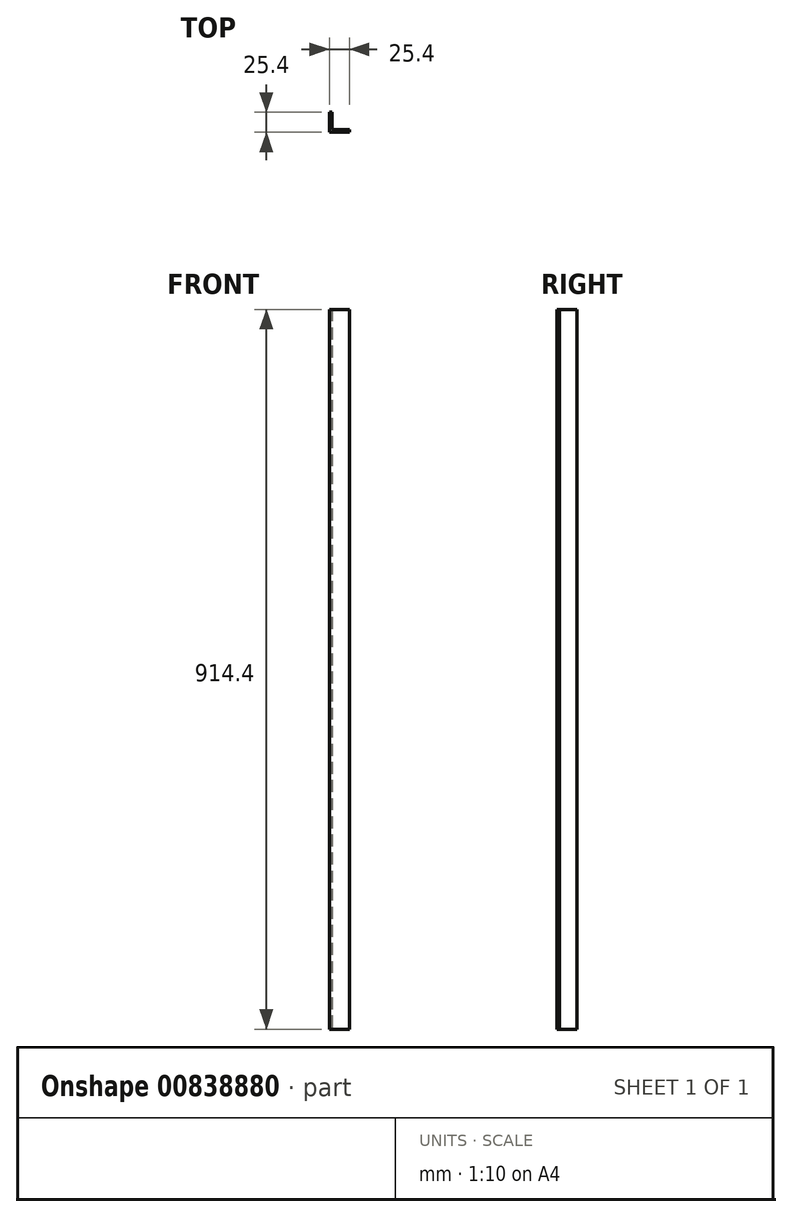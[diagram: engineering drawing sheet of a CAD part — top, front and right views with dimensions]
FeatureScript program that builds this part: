
annotation { "Feature Type Name" : "Feature", "Feature Type Description" : "" }
export const myFeature = defineFeature(function(context is Context, id is Id, definition is map)
    precondition{}
    {
        {
            var Q0;
            Q0=qCreatedBy(makeId("Top.planeOp"),FACE);
            var sketch = newSketch(context, id + "F0", { "sketchPlane" : qUnion([Q0])});
            skLineSegment(sketch, "E0", {"start": v(0, 0) * mm, "end": v(0, 25.4) * mm});
            skLineSegment(sketch, "E1", {"start": v(0, 25.4) * mm, "end": v(3.17, 25.4) * mm});
            skLineSegment(sketch, "E2", {"start": v(3.17, 25.4) * mm, "end": v(3.18, 3.17) * mm});
            skLineSegment(sketch, "E3", {"start": v(3.18, 3.17) * mm, "end": v(25.4, 3.18) * mm});
            skLineSegment(sketch, "E4", {"start": v(25.4, 3.18) * mm, "end": v(25.4, 0) * mm});
            skLineSegment(sketch, "E5", {"start": v(25.4, 0) * mm, "end": v(0, 0) * mm});
            skSolve(sketch);
        }
        {
            var Q0;
            Q0=makeQuery(id+"F0.imprint","IMPRINT",FACE,{"disambiguationData":[TD([[makeQuery(id+"F0.imprint","IMPRINT",EDGE,{"derivedFrom":sQuery(id+"F0.wireOp",EDGE,"E0")}),-1.0]])]});
            extrude(context, id + "F1", {"entities" : qUnion([Q0]), "depth" : 914.4 * mm, "offsetDistance" : 25.4 * mm});
        }
    });
